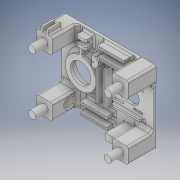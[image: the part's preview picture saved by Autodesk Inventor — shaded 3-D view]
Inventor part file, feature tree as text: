
AUTODESK INVENTOR PART (.ipt)
format: ipt  version: 2018 (Build 220112000, 112)  size: 873,472 bytes
history: native  units: in
note: dims shown in document units (in); Inventor stores cm internally (conversion verified against a paired STEP export)
features: extrude x23, fillet x18, sketch x13, emboss x1, chamfer x1, hole x1
ambient origin geometry x8: Origin, YZ Plane, XZ Plane, XY Plane, X Axis, Y Axis, Z Axis, Center Point
bodies: Solid1 (feature_tree)
feature tree (57):
  sketch  "Sketch1"  dims[d0=4.7244in d1=3.5433in]
  extrude  "Extrusion1"  Depth=3.5433in
  extrude  "Extrusion2"  Depth=4.5276in
  extrude  "Extrusion5"  Depth=1.6634in
  extrude  "Extrusion6"  Depth=1.6654in
  extrude  "Extrusion8"  Depth=1.2205in
  extrude  "Extrusion9"  Depth=0.1181in
  fillet  "Fillet1"  Radius=0.1181in
  fillet  "Fillet2"  Radius=0.1181in
  fillet  "Fillet3"  Radius=0.1181in
  extrude  "Extrusion10"  Depth=1.7323in TaperAngle=0.0deg
  sketch  "Sketch4"  dims[d12=1.3287in d13=1.6654in]
  extrude  "Extrusion11"  Depth=0.3937in TaperAngle=0.0deg
  fillet  "Fillet4"  Radius=1.1276in
  extrude  "Extrusion12"  Depth=0.3543in TaperAngle=0.0deg
  fillet  "Fillet5"  Radius=0.315in
  extrude  "Extrusion14"  Depth=1.3287in
  extrude  "Extrusion15"  Depth=4.7244in
  extrude  "Extrusion16"  Depth=0.4429in
  fillet  "Fillet7"  Radius=0.4429in
  fillet  "Fillet8"  Radius=0.4429in
  extrude  "Extrusion17"  Depth=0.0787in TaperAngle=0.0deg
  extrude  "Extrusion18"  Depth=0.0787in
  extrude  "Extrusion19"  Depth=0.0787in
  emboss  "Emboss1"
  extrude  "Extrusion20"  Depth=0.0787in
  extrude  "Extrusion21"  Depth=0.0787in
  extrude  "Extrusion22"  Depth=0.0787in
  fillet  "Fillet9"  Radius=0.5906in
  extrude  "Extrusion23"  Depth=0.0787in
  fillet  "Fillet10"  Radius=0.1772in
  sketch  "Sketch13"  dims[d35=0.1181in d36=0.3543in d37=0.0in d41=0.315in]
  extrude  "Extrusion25"  Depth=0.0787in TaperAngle=0.0deg
  chamfer  "Chamfer1"  Distance=1.4764in
  fillet  "Fillet11"  Radius=0.0591in
  hole  "Hole1"  [1 undecoded]
  extrude  "Extrusion26"  Depth=0.0787in
  extrude  "Extrusion27"  Depth=0.0787in TaperAngle=0.0deg
  fillet  "Fillet12"  Radius=0.1181in
  fillet  "Fillet13"  Radius=1.1811in
  fillet  "Fillet14"  Radius=0.5906in
  fillet  "Fillet15"  Radius=0.5906in
  fillet  "Fillet16"  Radius=0.2362in
  fillet  "Fillet17"  Radius=0.1181in
  fillet  "Fillet18"  Radius=0.7874in
  extrude  "Extrusion28"  Depth=0.0787in
  fillet  "Fillet19"  Radius=1.378in
  sketch  "Sketch19"  dims[d48=3.5433in d49=0.4429in d50=0.4429in d51=0.4429in]
  sketch  "Sketch20"  dims[d52=0.4429in d53=0.7874in d54=0.0in d55=0.1181in d56=0.1969in d57=0.1969in d58=1.1811in d59=1.6535in d60=0.5906in d61=0.1772in d62=0.1772in d63=0.6299in d64=0.0in d65=1.4764in d66=0.0591in d67=1.4764in d68=0.0591in d69=0.0591in d70=0.0in d71=0.1181in d72=1.1811in d73=0.5906in d74=0.5906in d75=0.2362in d76=0.0in d77=0.1181in d82=0.7874in d83=0.3937in d84=1.378in d85=0.0in d87=0.2362in d88=0.2362in d89=0.2362in d90=0.2362in d91=0.9843in d92=0.0in d93=0.1181in d94=0.1181in d95=0.3543in d96=0.0in d97=0.1181in d99=1.9685in d100=0.9843in d105=0.4921in d107=0.0in d108=0.4921in d109=0.1181in d110=0.9449in d111=0.0in d112=0.0787in d113=0.3937in d114=0.3937in d115=0.3937in d116=0.3937in d117=0.3937in d118=0.3937in d119=0.7874in d120=0.0in d121=2.9331in d122=0.0787in d123=0.1181in d124=0.0in d125=1.9685in d126=0.7087in d127=0.0591in d128=0.0in d129=0.5906in d130=0.1969in d131=0.3937in d132=0.0in d133=0.1575in d134=0.1575in d135=0.3937in d136=0.0in d137=0.7874in d138=0.2165in d139=0.1181in d140=0.1181in d141=0.2756in d142=0.0in d143=0.0787in d144=0.0787in d145=1.9685in d146=0.0787in d147=2.1654in d148=0.4724in d149=0.0in d150=0.0787in d156=0.4331in d157=0.0787in d158=0.0787in d160=1.1811in d161=0.3937in d162=0.7087in d163=0.3937in d164=0.0in d165=0.1575in d166=0.0787in d167=45.0deg d168=0.1181in d169=1.1319in d170=0.0787in d171=0.0787in d172=0.2362in d173=0.1575in d174=0.0787in d175=90.0deg d176=0.1575in d177=0.8108in d178=1.6535in d179=0.5906in d180=0.1772in d181=0.1772in d182=0.7087in d183=0.6299in d184=0.0in d189=1.4764in d190=0.0591in d191=1.4764in d192=0.0591in d193=0.0591in d194=0.0in d195=0.1181in d197=1.1813in d198=0.0787in d199=0.0787in d200=0.0787in d201=0.0787in d202=0.0787in d203=0.0787in d204=0.2953in d205=0.5906in d206=0.0591in d207=0.0in d208=0.0787in]
  sketch  "Sketch2"  dims[d2=5.7087in d3=4.5276in]
  sketch  "Sketch3"  dims[d8=1.6634in d10=1.6634in]
  sketch  "Sketch6"  dims[d14=1.6654in d15=1.2205in]
  sketch  "Sketch7"  dims[d16=1.2205in d17=0.1181in d18=0.1181in d19=0.1181in d20=0.1181in]
  sketch  "Sketch8"  dims[d21=0.1575in d22=0.0in d23=1.7323in d24=0.0in]
  sketch  "Sketch9"  dims[d30=0.876in d31=0.3937in d32=0.0in d33=1.1276in]
  sketch  "Sketch16"  dims[d42=0.1575in d43=0.0in d45=1.3287in]
  sketch  "Sketch18"  dims[d46=0.5012in d47=4.7244in]
note: 1 required parameter value undecoded (feature->parameter linkage not recoverable at this tier; creation-order binding heuristic only, values carry confidence <= 0.55)
